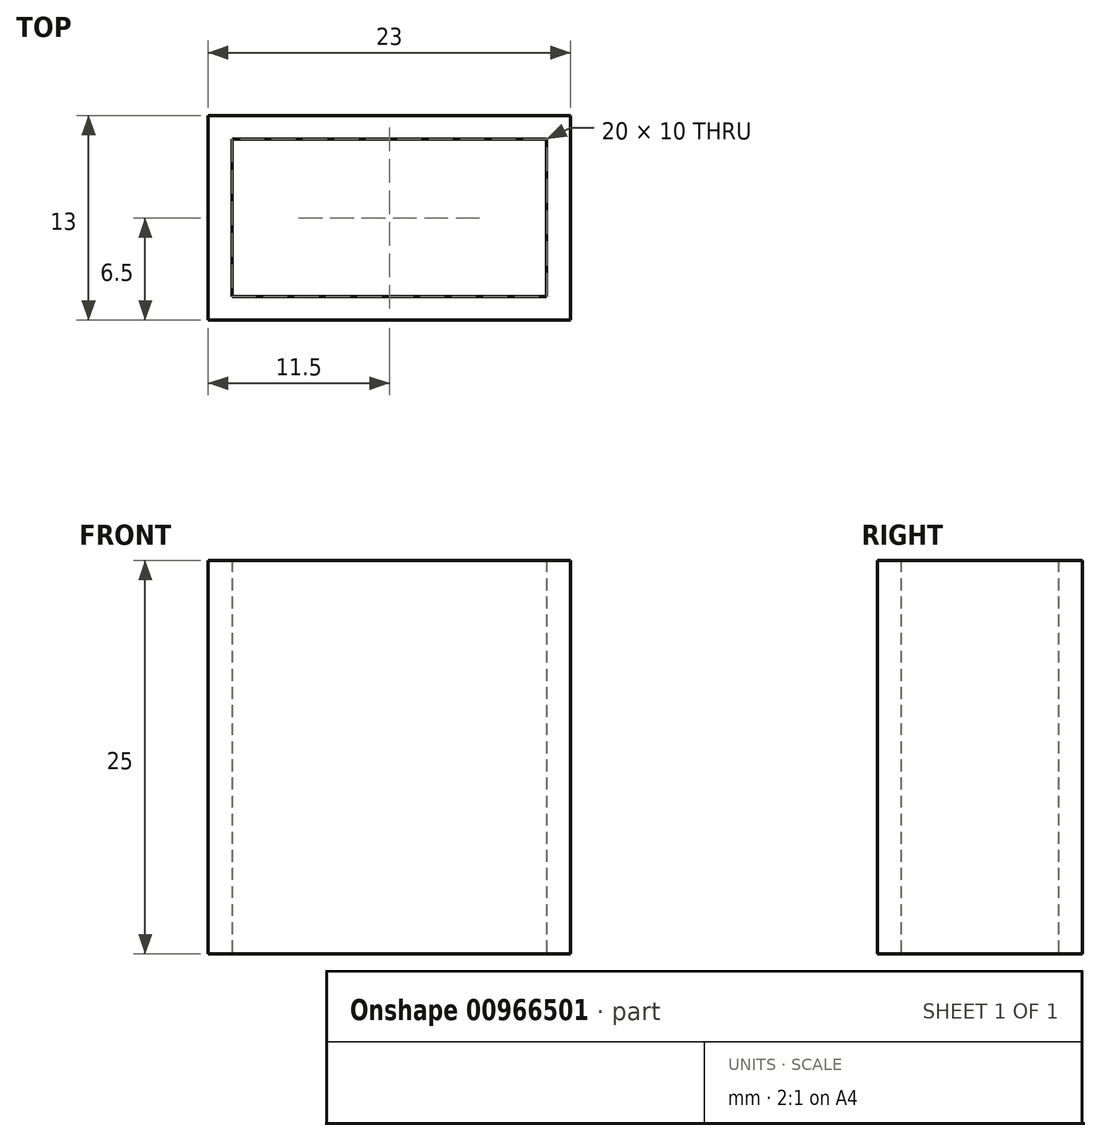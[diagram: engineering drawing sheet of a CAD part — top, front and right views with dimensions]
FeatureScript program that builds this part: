
annotation { "Feature Type Name" : "Feature", "Feature Type Description" : "" }
export const myFeature = defineFeature(function(context is Context, id is Id, definition is map)
    precondition{}
    {
        {
            var Q0;
            Q0=qCreatedBy(makeId("Top.planeOp"),FACE);
            var sketch = newSketch(context, id + "F0", { "sketchPlane" : qUnion([Q0])});
            skLineSegment(sketch, "E0.bottom", {"start": v(0, 0) * mm, "end": v(20, 0) * mm});
            skLineSegment(sketch, "E0.top", {"start": v(0, 10) * mm, "end": v(20, 10) * mm});
            skLineSegment(sketch, "E0.left", {"start": v(0, 0) * mm, "end": v(0, 10) * mm});
            skLineSegment(sketch, "E0.right", {"start": v(20, 0) * mm, "end": v(20, 10) * mm});
            skLineSegment(sketch, "E1.bottom", {"start": v(-1.5, 11.5) * mm, "end": v(21.5, 11.5) * mm});
            skLineSegment(sketch, "E1.top", {"start": v(-1.5, -1.5) * mm, "end": v(21.5, -1.5) * mm});
            skLineSegment(sketch, "E1.left", {"start": v(-1.5, 11.5) * mm, "end": v(-1.5, -1.5) * mm});
            skLineSegment(sketch, "E1.right", {"start": v(21.5, 11.5) * mm, "end": v(21.5, -1.5) * mm});
            skSolve(sketch);
        }
        {
            var Q0;
            Q0 = qSketchRegion(id + "F0", true);
            extrude(context, id + "F1", {"entities" : qUnion([Q0]), "depth" : 25 * mm, "offsetDistance" : 25 * mm});
        }
    });
